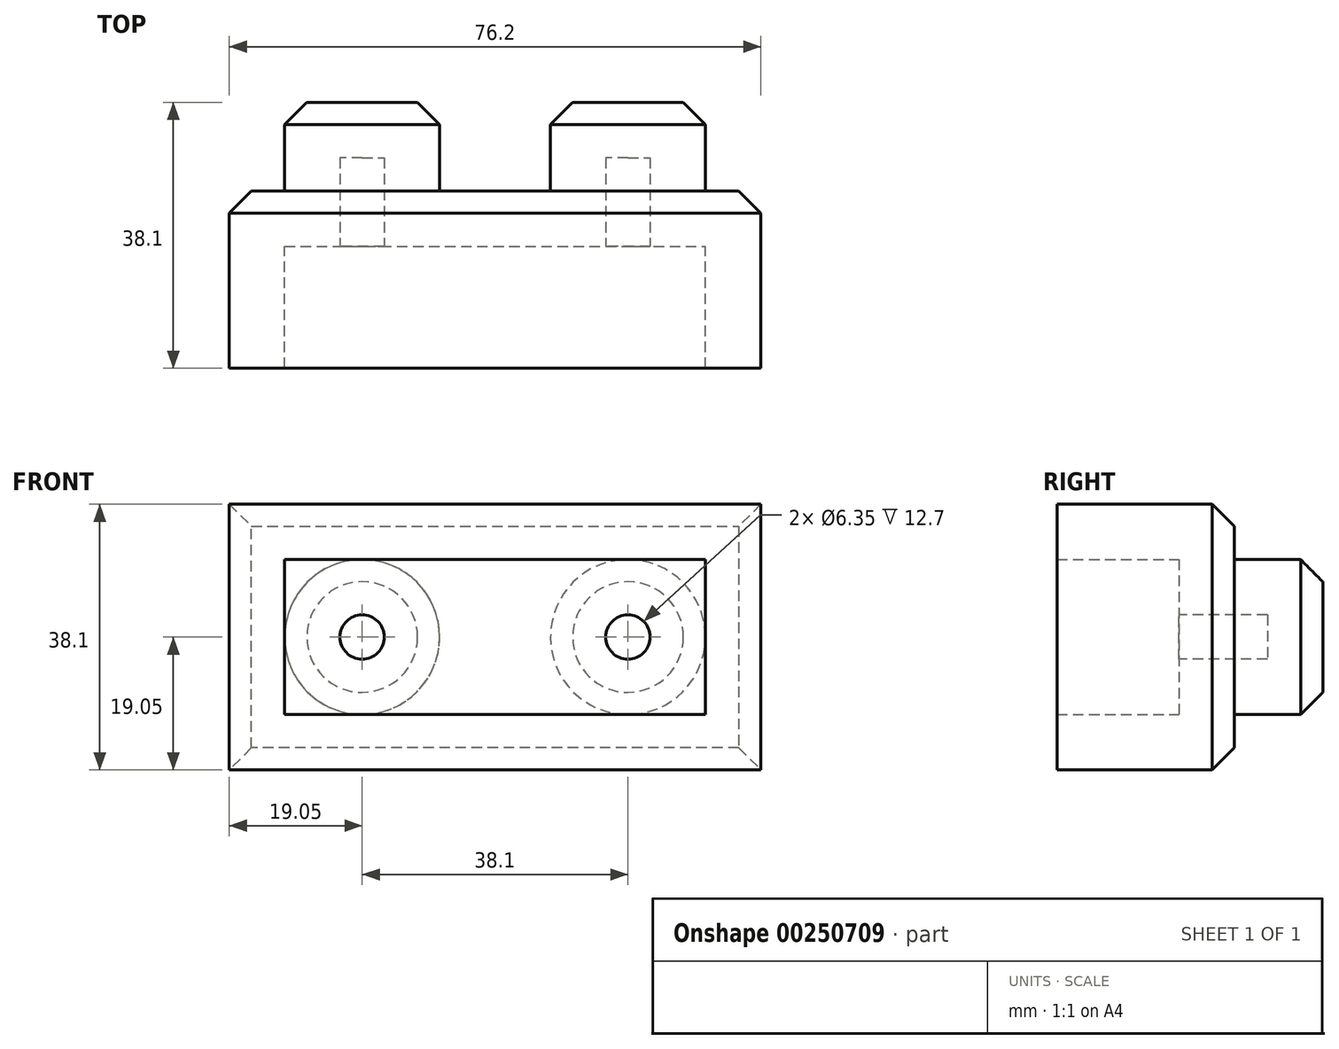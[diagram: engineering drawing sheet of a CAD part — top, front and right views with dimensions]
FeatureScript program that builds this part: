
annotation { "Feature Type Name" : "Feature", "Feature Type Description" : "" }
export const myFeature = defineFeature(function(context is Context, id is Id, definition is map)
    precondition{}
    {
        {
            var Q0;
            Q0=qCreatedBy(makeId("Front.planeOp"),FACE);
            var sketch = newSketch(context, id + "F0", { "sketchPlane" : qUnion([Q0])});
            skLineSegment(sketch, "E0.bottom", {"start": v(38.1, -19.05) * mm, "end": v(-38.1, -19.05) * mm});
            skLineSegment(sketch, "E0.top", {"start": v(38.1, 19.05) * mm, "end": v(-38.1, 19.05) * mm});
            skLineSegment(sketch, "E0.left", {"start": v(38.1, -19.05) * mm, "end": v(38.1, 19.05) * mm});
            skLineSegment(sketch, "E0.right", {"start": v(-38.1, -19.05) * mm, "end": v(-38.1, 19.05) * mm});
            skPoint(sketch, "E0.middle", {"position": v(0, 0) * mm});
            skSolve(sketch);
        }
        {
            var Q0;
            Q0=makeQuery(id+"F0.imprint","IMPRINT",FACE,{"disambiguationData":[TD([[makeQuery(id+"F0.imprint","IMPRINT",EDGE,{"derivedFrom":sQuery(id+"F0.wireOp",EDGE,"E0.bottom")}),-1.0]])]});
            extrude(context, id + "F1", {"entities" : qUnion([Q0]), "depth" : 25.4 * mm});
        }
        {
            var Q0;
            Q0=makeQuery(id+"F1.opExtrude","CAP_FACE",FACE,{"disambiguationData":[OSD([sQuery(id+"F0.wireOp",EDGE,"E0.bottom"),sQuery(id+"F0.wireOp",EDGE,"E0.top"),sQuery(id+"F0.wireOp",EDGE,"E0.left"),sQuery(id+"F0.wireOp",EDGE,"E0.right")])],"isStart":true});
            var sketch = newSketch(context, id + "F2", { "sketchPlane" : qUnion([Q0])});
            skCircle(sketch, "E1", {"center": v(-19.05, 0) * mm, "radius": 11.11 * mm});
            skCircle(sketch, "E2", {"center": v(19.05, 0) * mm, "radius": 11.11 * mm});
            skSolve(sketch);
        }
        {
            var Q0;
            Q0=makeQuery(id+"F2.imprint","IMPRINT",FACE,{"disambiguationData":[TD([[makeQuery(id+"F2.imprint","IMPRINT",EDGE,{"derivedFrom":sQuery(id+"F2.wireOp",EDGE,"E1")}),1.0]])]});
            var Q1;
            Q1=makeQuery(id+"F2.imprint","IMPRINT",FACE,{"disambiguationData":[TD([[makeQuery(id+"F2.imprint","IMPRINT",EDGE,{"derivedFrom":sQuery(id+"F2.wireOp",EDGE,"E2")}),1.0]])]});
            extrude(context, id + "F3", {"entities" : qUnion([Q0, Q1]), "operationType" : NewBodyOperationType.ADD, "depth" : 12.7 * mm});
        }
        {
            var Q0;
            Q0=makeQuery(id+"F3.opExtrude","CAP_EDGE",EDGE,{"disambiguationData":[OSD([sQuery(id+"F2.wireOp",EDGE,"E2")])],"isStart":false});
            var Q1;
            Q1=makeQuery(id+"F3.opExtrude","CAP_EDGE",EDGE,{"disambiguationData":[OSD([sQuery(id+"F2.wireOp",EDGE,"E1")])],"isStart":false});
            var Q2;
            Q2=makeQuery(id+"F1.opExtrude","CAP_EDGE",EDGE,{"disambiguationData":[OSD([sQuery(id+"F0.wireOp",EDGE,"E0.top")])],"isStart":true});
            var Q3;
            Q3=makeQuery(id+"F1.opExtrude","CAP_EDGE",EDGE,{"disambiguationData":[OSD([sQuery(id+"F0.wireOp",EDGE,"E0.left")])],"isStart":true});
            var Q4;
            Q4=makeQuery(id+"F1.opExtrude","CAP_EDGE",EDGE,{"disambiguationData":[OSD([sQuery(id+"F0.wireOp",EDGE,"E0.right")])],"isStart":true});
            var Q5;
            Q5=makeQuery(id+"F1.opExtrude","CAP_EDGE",EDGE,{"disambiguationData":[OSD([sQuery(id+"F0.wireOp",EDGE,"E0.bottom")])],"isStart":true});
            chamfer(context, id + "F4", {"entities" : qUnion([Q0, Q1, Q2, Q3, Q4, Q5]), "chamferType" : ChamferType.OFFSET_ANGLE, "width" : 3.17 * mm, "oppositeDirection" : false, "angle" : 45 * degree, "tangentPropagation" : true});
        }
        {
            var Q0;
            Q0=makeQuery(id+"F1.opExtrude","CAP_FACE",FACE,{"disambiguationData":[OSD([sQuery(id+"F0.wireOp",EDGE,"E0.bottom"),sQuery(id+"F0.wireOp",EDGE,"E0.top"),sQuery(id+"F0.wireOp",EDGE,"E0.left"),sQuery(id+"F0.wireOp",EDGE,"E0.right")])],"isStart":false});
            shell(context, id + "F5", {"entities" : qUnion([Q0]), "thickness" : 7.94 * mm});
        }
    });
